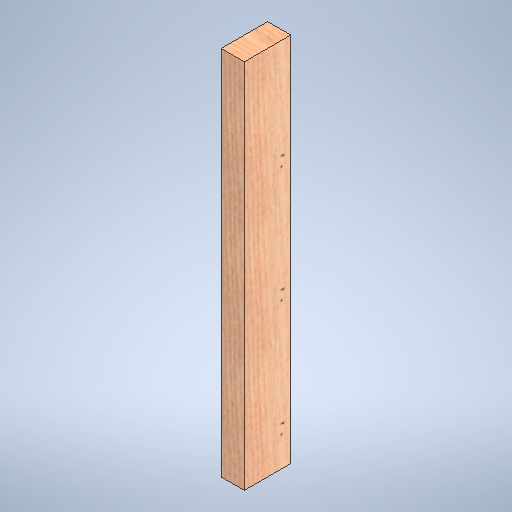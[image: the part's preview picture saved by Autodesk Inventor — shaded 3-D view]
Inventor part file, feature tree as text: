
AUTODESK INVENTOR PART (.ipt)
format: ipt  version: 2025 (Build 290162000, 162)  size: 334,336 bytes
history: native  units: in
note: dims shown in document units (in); Inventor stores cm internally (conversion verified against a paired STEP export)
features: extrude x1, sketch x1
ambient origin geometry x8: Origin, YZ Plane, XZ Plane, XY Plane, X Axis, Y Axis, Z Axis, Center Point
bodies: Solid1 (feature_tree)
feature tree (2):
  extrude  "Extrusion1"  Depth=4.0in
  sketch  "Sketch1"  dims[d0=2.0in d1=4.0in d2=32.0in d3=0.0in]
